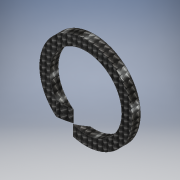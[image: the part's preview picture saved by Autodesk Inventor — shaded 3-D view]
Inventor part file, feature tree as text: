
AUTODESK INVENTOR PART (.ipt)
format: ipt  version: 2017 (Build 210142000, 142)  size: 133,120 bytes
history: native  units: mm
features: extrude x2, chamfer x2, sketch x2
ambient origin geometry x8: Origin, YZ Plane, XZ Plane, XY Plane, X Axis, Y Axis, Z Axis, Center Point
bodies: Body1 (feature_tree)
feature tree (6):
  extrude  "Extrusion3"  Depth=3.0mm TaperAngle=0.0deg
  extrude  "Extrusion4"  TaperAngle=0.0deg  [1 undecoded]
  chamfer  "Chamfer3"  Distance=3.0mm Angle=45.0deg
  chamfer  "Chamfer4"  Distance=3.0mm Angle=45.0deg
  sketch  "Sketch1"  dims[d74=32.0mm d75=3.0mm d76=0.0mm]
  sketch  "Sketch4"  dims[d77=25.0mm d78=0.0mm d79=0.0mm d86=3.0mm d87=2.0mm d88=45.0deg d89=3.0mm d90=2.0mm d91=45.0deg]
note: 1 required parameter value undecoded (feature->parameter linkage not recoverable at this tier; creation-order binding heuristic only, values carry confidence <= 0.55)
